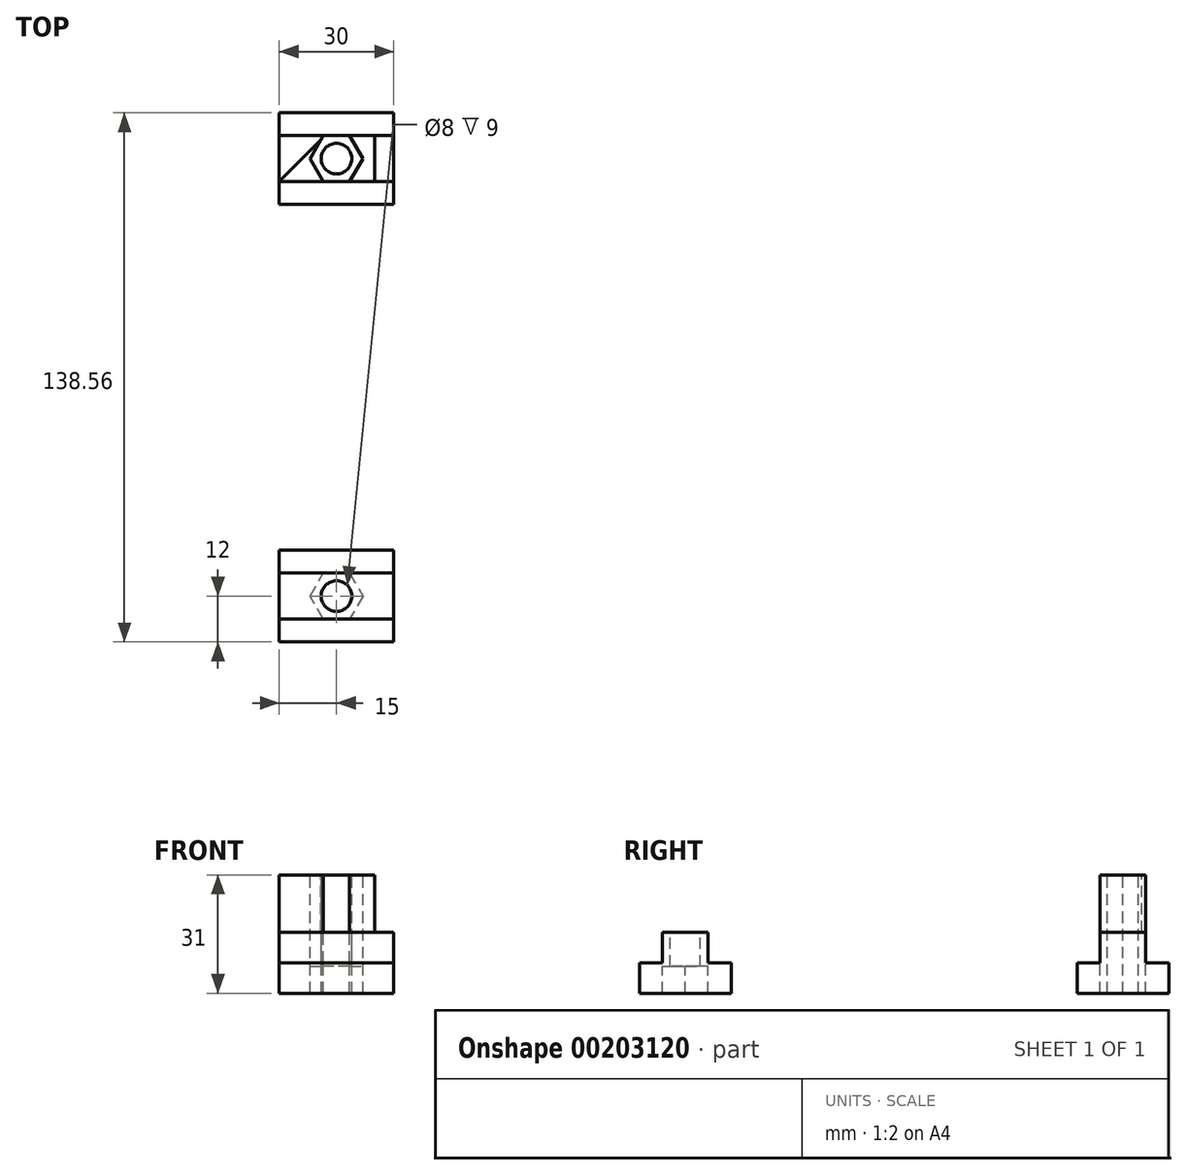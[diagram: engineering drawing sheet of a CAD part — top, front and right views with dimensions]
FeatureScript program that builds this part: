
annotation { "Feature Type Name" : "Feature", "Feature Type Description" : "" }
export const myFeature = defineFeature(function(context is Context, id is Id, definition is map)
    precondition{}
    {
        {
            var Q0;
            Q0=qCreatedBy(makeId("Right.planeOp"),FACE);
            var sketch = newSketch(context, id + "F0", { "sketchPlane" : qUnion([Q0])});
            skLineSegment(sketch, "E0.bottom", {"start": v(0, 0) * mm, "end": v(1500, 0) * mm, "construction": true});
            skLineSegment(sketch, "E0.top", {"start": v(0, 1000) * mm, "end": v(1500, 1000) * mm, "construction": true});
            skLineSegment(sketch, "E0.left", {"start": v(0, 0) * mm, "end": v(0, 1000) * mm, "construction": true});
            skLineSegment(sketch, "E0.right", {"start": v(1500, 0) * mm, "end": v(1500, 1000) * mm, "construction": true});
            skLineSegment(sketch, "E1.bottom", {"start": v(30.75, 3.6) * mm, "end": v(36.75, 3.6) * mm});
            skLineSegment(sketch, "E1.top", {"start": v(30.75, 11.6) * mm, "end": v(36.75, 11.6) * mm});
            skLineSegment(sketch, "E1.left", {"start": v(30.75, 3.6) * mm, "end": v(30.75, 11.6) * mm});
            skLineSegment(sketch, "E1.right", {"start": v(36.75, 3.6) * mm, "end": v(36.75, 11.6) * mm});
            skLineSegment(sketch, "E2.bottom", {"start": v(36.75, 11.6) * mm, "end": v(48.75, 11.6) * mm});
            skLineSegment(sketch, "E2.top", {"start": v(36.75, 19.6) * mm, "end": v(48.75, 19.6) * mm});
            skLineSegment(sketch, "E2.left", {"start": v(36.75, 11.6) * mm, "end": v(36.75, 19.6) * mm});
            skLineSegment(sketch, "E2.right", {"start": v(48.75, 11.6) * mm, "end": v(48.75, 19.6) * mm});
            skLineSegment(sketch, "E3.bottom", {"start": v(48.75, 11.6) * mm, "end": v(54.75, 11.6) * mm});
            skLineSegment(sketch, "E3.top", {"start": v(48.75, 3.6) * mm, "end": v(54.75, 3.6) * mm});
            skLineSegment(sketch, "E3.left", {"start": v(48.75, 11.6) * mm, "end": v(48.75, 3.6) * mm});
            skLineSegment(sketch, "E3.right", {"start": v(54.75, 11.6) * mm, "end": v(54.75, 3.6) * mm});
            skPoint(sketch, "E4", {"position": v(42.75, 19.6) * mm});
            skPoint(sketch, "E5", {"position": v(42.75, 0) * mm});
            skLineSegment(sketch, "E6", {"start": v(36.75, 3.6) * mm, "end": v(48.75, 3.6) * mm});
            skLineSegment(sketch, "E7", {"start": v(100.03, -3.57) * mm, "end": v(100.03, -42.2) * mm, "construction": true});
            skLineSegment(sketch, "E8.MirrorCS", {"start": v(151.3, 11.6) * mm, "end": v(151.3, 3.6) * mm});
            skLineSegment(sketch, "E9.MirrorCS", {"start": v(163.3, 3.6) * mm, "end": v(163.3, 11.6) * mm});
            skLineSegment(sketch, "E10.MirrorCS", {"start": v(169.3, 3.6) * mm, "end": v(163.3, 3.6) * mm});
            skLineSegment(sketch, "E11.MirrorCS", {"start": v(151.3, 11.6) * mm, "end": v(145.3, 11.6) * mm});
            skLineSegment(sketch, "E12.MirrorCS", {"start": v(145.3, 11.6) * mm, "end": v(145.3, 3.6) * mm});
            skLineSegment(sketch, "E13.MirrorCS", {"start": v(169.3, 11.6) * mm, "end": v(163.3, 11.6) * mm});
            skLineSegment(sketch, "E14.MirrorCS", {"start": v(169.3, 3.6) * mm, "end": v(169.3, 11.6) * mm});
            skLineSegment(sketch, "E15.MirrorCS", {"start": v(151.3, 3.6) * mm, "end": v(145.3, 3.6) * mm});
            skLineSegment(sketch, "E16.MirrorCS", {"start": v(163.3, 3.6) * mm, "end": v(151.3, 3.6) * mm});
            skLineSegment(sketch, "E17.MirrorCS", {"start": v(163.3, 19.6) * mm, "end": v(151.3, 19.6) * mm});
            skLineSegment(sketch, "E18.MirrorCS", {"start": v(163.3, 11.6) * mm, "end": v(151.3, 11.6) * mm});
            skLineSegment(sketch, "E19.MirrorCS", {"start": v(163.3, 11.6) * mm, "end": v(163.3, 19.6) * mm});
            skPoint(sketch, "E20.MirrorP", {"position": v(157.3, 19.6) * mm});
            skPoint(sketch, "E21.MirrorP", {"position": v(157.3, 0) * mm});
            skLineSegment(sketch, "E22.MirrorCS", {"start": v(151.3, 11.6) * mm, "end": v(151.3, 19.6) * mm});
            skSolve(sketch);
        }
        {
            var Q0;
            Q0 = qSketchRegion(id + "F0", true);
            extrude(context, id + "F1", {"entities" : qUnion([Q0]), "depth" : 30 * mm});
        }
        {
            var Q0;
            Q0=makeQuery(id+"F1.opExtrude","SWEPT_FACE",FACE,{"disambiguationData":[OSD([sQuery(id+"F0.wireOp",EDGE,"E2.top")])]});
            var sketch = newSketch(context, id + "F2", { "sketchPlane" : qUnion([Q0])});
            skCircle(sketch, "E23", {"center": v(15, 42.75) * mm, "radius": 4 * mm});
            skPoint(sketch, "E23.centerSnap0", {"position": v(0, 42.75) * mm});
            skPoint(sketch, "E23.centerSnap1", {"position": v(15, 36.75) * mm});
            skCircle(sketch, "E24.cCircle", {"center": v(15, 42.75) * mm, "radius": 6 * mm, "construction": true});
            skPoint(sketch, "E24.cCircle.perimeterSnap0", {"position": v(15, 48.75) * mm});
            skLineSegment(sketch, "E24.0", {"start": v(11.54, 48.75) * mm, "end": v(18.46, 48.75) * mm});
            skLineSegment(sketch, "E24.1", {"start": v(18.46, 48.75) * mm, "end": v(21.93, 42.75) * mm});
            skLineSegment(sketch, "E24.2", {"start": v(21.93, 42.75) * mm, "end": v(18.46, 36.75) * mm});
            skLineSegment(sketch, "E24.3", {"start": v(18.46, 36.75) * mm, "end": v(11.54, 36.75) * mm});
            skLineSegment(sketch, "E24.4", {"start": v(11.54, 36.75) * mm, "end": v(8.07, 42.75) * mm});
            skLineSegment(sketch, "E24.5", {"start": v(8.07, 42.75) * mm, "end": v(11.54, 48.75) * mm});
            skPoint(sketch, "E24.0.midPoint", {"position": v(15, 48.75) * mm});
            skPoint(sketch, "E24.0.midPoint.positionSnap0", {"position": v(15, 48.75) * mm});
            skLineSegment(sketch, "E25", {"start": v(-69.7, 100.03) * mm, "end": v(0, 100.03) * mm, "construction": true});
            skLineSegment(sketch, "E26.MirrorCS", {"start": v(18.46, 163.3) * mm, "end": v(11.54, 163.3) * mm});
            skLineSegment(sketch, "E27.MirrorCS", {"start": v(18.46, 151.3) * mm, "end": v(21.93, 157.3) * mm});
            skLineSegment(sketch, "E28.MirrorCS", {"start": v(21.93, 157.3) * mm, "end": v(18.46, 163.3) * mm});
            skLineSegment(sketch, "E29.MirrorCS", {"start": v(8.07, 157.3) * mm, "end": v(11.54, 151.3) * mm});
            skLineSegment(sketch, "E30.MirrorCS", {"start": v(11.54, 163.3) * mm, "end": v(8.07, 157.3) * mm});
            skCircle(sketch, "E31.MirrorC", {"center": v(15, 157.3) * mm, "radius": 6 * mm, "construction": true});
            skCircle(sketch, "E32.MirrorC", {"center": v(15, 157.3) * mm, "radius": 4 * mm});
            skLineSegment(sketch, "E33.MirrorCS", {"start": v(11.54, 151.3) * mm, "end": v(18.46, 151.3) * mm});
            skSolve(sketch);
        }
        {
            var Q0;
            Q0=makeQuery(id+"F2.imprint","IMPRINT",FACE,{"disambiguationData":[TD([[makeQuery(id+"F2.imprint","IMPRINT",EDGE,{"derivedFrom":sQuery(id+"F2.wireOp",EDGE,"E23")}),-1.0]])]});
            var Q1;
            Q1=makeQuery(id+"F2.imprint","IMPRINT",FACE,{"disambiguationData":[TD([[makeQuery(id+"F2.imprint","IMPRINT",EDGE,{"derivedFrom":sQuery(id+"F2.wireOp",EDGE,"E27.MirrorCS")}),1.0]])]});
            extrude(context, id + "F3", {"entities" : qUnion([Q0, Q1]), "operationType" : NewBodyOperationType.REMOVE, "oppositeDirection" : true, "depth" : 17 * mm, "hasSecondDirection" : true, "secondDirectionOppositeDirection" : true, "secondDirectionDepth" : 9 * mm});
        }
        {
            var Q0;
            Q0=makeQuery(id+"F2.imprint","IMPRINT",FACE,{"disambiguationData":[TD([[makeQuery(id+"F2.imprint","IMPRINT",EDGE,{"derivedFrom":sQuery(id+"F2.wireOp",EDGE,"E23")}),1.0]])]});
            var Q1;
            Q1=makeQuery(id+"F2.imprint","IMPRINT",FACE,{"disambiguationData":[TD([[makeQuery(id+"F2.imprint","IMPRINT",EDGE,{"derivedFrom":sQuery(id+"F2.wireOp",EDGE,"E32.MirrorC")}),-1.0]])]});
            extrude(context, id + "F4", {"entities" : qUnion([Q0, Q1]), "operationType" : NewBodyOperationType.REMOVE, "oppositeDirection" : true, "depth" : 40 * mm});
        }
        {
            var Q0;
            Q0=makeQuery(id+"F1.opExtrude","SWEPT_FACE",FACE,{"disambiguationData":[OSD([sQuery(id+"F0.wireOp",EDGE,"E17.MirrorCS")])]});
            extrude(context, id + "F5", {"entities" : qUnion([Q0]), "operationType" : NewBodyOperationType.ADD, "depth" : 15 * mm});
        }
        {
            var Q0;
            Q0=makeQuery(id+"F5.opExtrude","CAP_FACE",FACE,{"disambiguationData":[OSD([sQuery(id+"F0.wireOp",EDGE,"E17.MirrorCS")])],"isStart":false});
            var sketch = newSketch(context, id + "F6", { "sketchPlane" : qUnion([Q0])});
            skLineSegment(sketch, "E34", {"start": v(0, 151.3) * mm, "end": v(12, 163.3) * mm});
            skLineSegment(sketch, "E35.bottom", {"start": v(30, 163.3) * mm, "end": v(25, 163.3) * mm});
            skLineSegment(sketch, "E35.top", {"start": v(30, 151.3) * mm, "end": v(25, 151.3) * mm});
            skLineSegment(sketch, "E35.left", {"start": v(30, 163.3) * mm, "end": v(30, 151.3) * mm});
            skLineSegment(sketch, "E35.right", {"start": v(25, 163.3) * mm, "end": v(25, 151.3) * mm});
            skLineSegment(sketch, "E36", {"start": v(0, 151.3) * mm, "end": v(0, 163.3) * mm});
            skLineSegment(sketch, "E37", {"start": v(0, 163.3) * mm, "end": v(12, 163.3) * mm});
            skLineSegment(sketch, "E38", {"start": v(1.5, 151.3) * mm, "end": v(1.5, 152.8) * mm});
            skSolve(sketch);
        }
        {
            var Q0;
            Q0=makeQuery(id+"F6.imprint","IMPRINT",FACE,{"disambiguationData":[TD([[makeQuery(id+"F6.imprint","IMPRINT",EDGE,{"derivedFrom":sQuery(id+"F6.wireOp",EDGE,"E34")}),1.0]])]});
            var Q1;
            Q1=makeQuery(id+"F6.imprint","IMPRINT",FACE,{"disambiguationData":[TD([[makeQuery(id+"F6.imprint","IMPRINT",EDGE,{"derivedFrom":sQuery(id+"F6.wireOp",EDGE,"E35.bottom")}),1.0]])]});
            var Q2;
            {var subQ3=sQuery(id+"F6.wireOp",EDGE,"E38");Q2=makeQuery(id+"F6.imprint","IMPRINT",FACE,{"disambiguationData":[TD([[makeQuery(id+"F6.imprint","IMPRINT",EDGE,{"derivedFrom":subQ3}),1.0]])]});}
            extrude(context, id + "F7", {"entities" : qUnion([Q0, Q1, Q2]), "operationType" : NewBodyOperationType.REMOVE, "oppositeDirection" : true, "depth" : 15 * mm});
        }
    });
